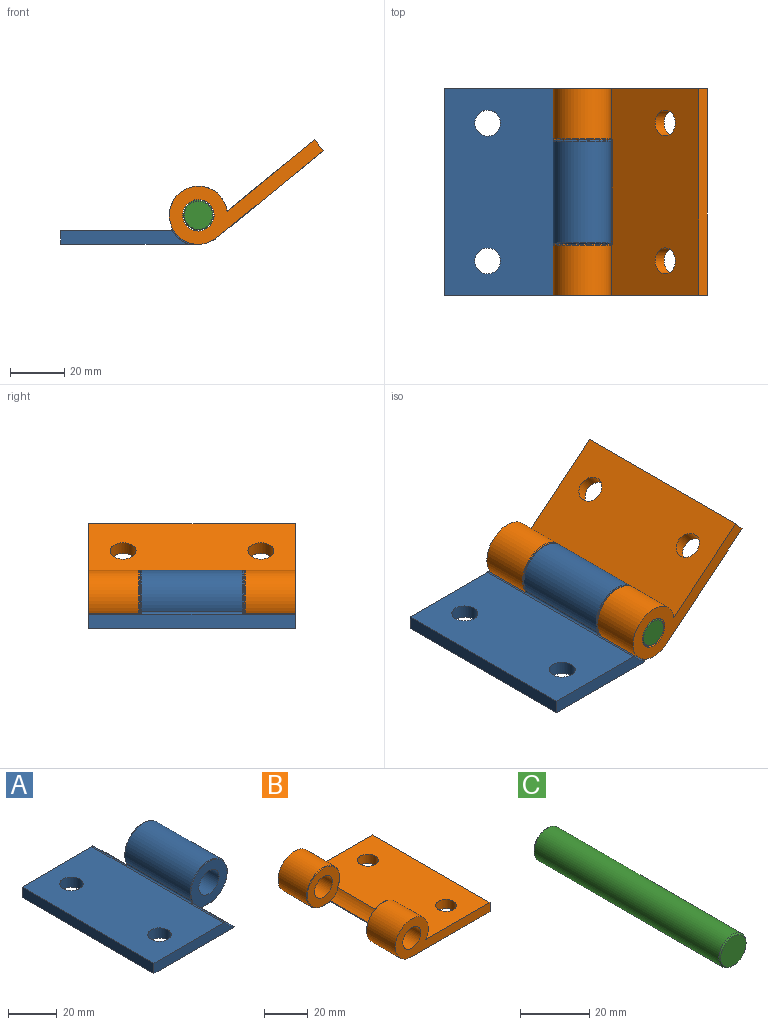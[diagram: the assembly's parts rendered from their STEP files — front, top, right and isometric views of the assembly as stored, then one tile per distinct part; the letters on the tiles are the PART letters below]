
ASSEMBLY  parts=3 mates=2
PART A: 23 faces, bbox 62.4x76.2x23.2 mm
  f0: cylinder r=1.59mm len=4.9mm, axis (-1,0,0), area 48.8mm2, adj f7,f8
  f1: cylinder r=4.76mm len=9.53mm, axis (0,0,1), area 154.3mm2, adj f10,f14
  f2: cylinder r=4.76mm len=9.53mm, axis (0,0,1), area 154.3mm2, adj f10,f14
  f3: torus R=10.45mm, axis (0,-1,0), area 21.8mm2, adj f4,f8,f16,f22
  f4: torus R=1.05mm, axis (0,-1,0), area 0.5mm2, adj f3,f11,f15,f16
  f5: torus R=10.45mm, axis (0,1,0), area 21.8mm2, adj f8,f18,f20,f21
  f6: cylinder r=0.25mm len=19.3mm, axis (0,-1,0), area 13.1mm2, adj f10,f12,f15,f16,f22
  f7: cylinder r=5.81mm len=38.1mm, axis (0,1,0), area 1382.9mm2, adj f0,f16,f18
  f8: cylinder r=10.71mm len=37.59mm, axis (0,1,0), area 2060.3mm2, adj f0,f3,f5,f10,f11
  f9: plane 46.2x5.37mm, normal (0,1,0), area 223.2mm2, adj f10,f11,f13,f14,f17,f19
  f10: plane 76.2x50.8mm, normal (0,0,-1), area 3541mm2, adj f1,f2,f6,f8,f9,f12,f13,f19
  f11: cylinder r=0.79mm len=76.2mm, axis (0,1,0), area 82.6mm2, adj f4,f8,f9,f12,f14,f15,f17,f21
  f12: plane 46.2x5.37mm, normal (0,-1,0), area 223.2mm2, adj f6,f10,f11,f13,f14,f15
  f13: plane 76.2x5.16mm, normal (-1,0,0), area 392.9mm2, adj f9,f10,f12,f14
  f14: plane 76.2x40.33mm, normal (0,0,1), area 2930.6mm2, adj f1,f2,f9,f11,f12,f13
  f15: cylinder r=11.27mm len=19.3mm, axis (0,-1,0), area 138mm2, adj f4,f6,f11,f12,f16
  f16: plane 20.9x20.9mm, normal (0,-1,0), area 244.4mm2, adj f3,f4,f6,f7,f15,f22
  f17: cylinder r=11.27mm len=19.3mm, axis (0,1,0), area 138mm2, adj f9,f11,f18,f19,f21
  f18: plane 20.9x20.9mm, normal (0,1,0), area 244.4mm2, adj f5,f7,f17,f19,f20,f21
  f19: cylinder r=0.25mm len=19.3mm, axis (0,1,0), area 13.1mm2, adj f9,f10,f17,f18,f20
  f20: cylinder r=0.25mm len=4.86mm, axis (1,0,0), area 1.9mm2, adj f5,f10,f18,f19
  f21: torus R=1.05mm, axis (0,1,0), area 0.5mm2, adj f5,f11,f17,f18
  f22: cylinder r=0.25mm len=4.86mm, axis (-1,0,0), area 1.9mm2, adj f3,f6,f10,f16
PART B: 19 faces, bbox 62.5x76.3x23.2 mm
  f0: cylinder r=4.76mm len=9.53mm, axis (0,0,1), area 154.3mm2, adj f10,f11
  f1: cylinder r=4.76mm len=9.53mm, axis (0,0,1), area 154.3mm2, adj f10,f11
  f2: torus R=10.45mm, axis (0,1,0), area 22.3mm2, adj f4,f11,f16,f18
  f3: cylinder r=5.81mm len=18.8mm, axis (0,1,0), area 686.2mm2, adj f16,f17
  f4: cylinder r=10.71mm len=21.41mm, axis (0,1,0), area 1043.7mm2, adj f2,f10,f11,f17
  f5: torus R=10.45mm, axis (0,-1,0), area 22.3mm2, adj f7,f8,f11,f15
  f6: cylinder r=5.81mm len=18.8mm, axis (0,-1,0), area 686.2mm2, adj f8,f12
  f7: cylinder r=10.71mm len=21.41mm, axis (0,-1,0), area 1043.7mm2, adj f5,f10,f11,f12
  f8: plane 20.9x20.9mm, normal (0,1,0), area 244.1mm2, adj f5,f6,f11,f13,f14,f15
  f9: plane 76.2x5.16mm, normal (1,0,0), area 392.9mm2, adj f10,f11,f12,f17
  f10: plane 76.2x50.8mm, normal (0,0,-1), area 3538.5mm2, adj f0,f1,f4,f7,f9,f12,f14,f15
  f11: plane 76.26x42.01mm, normal (0,0,1), area 3005.6mm2, adj f0,f1,f2,f4,f5,f7,f8,f9
  f12: plane 61.51x21.41mm, normal (0,-1,0), area 482.6mm2, adj f6,f7,f9,f10,f11
  f13: cylinder r=11.27mm len=38.61mm, axis (0,-1,0), area 270.2mm2, adj f8,f11,f14,f16
  f14: cylinder r=0.25mm len=39.12mm, axis (0,-1,0), area 26.6mm2, adj f8,f10,f13,f15,f16,f18
  f15: cylinder r=0.25mm len=4.86mm, axis (-1,0,0), area 1.9mm2, adj f5,f8,f10,f14
  f16: plane 20.9x20.9mm, normal (0,-1,0), area 244.1mm2, adj f2,f3,f11,f13,f14,f18
  f17: plane 61.51x21.41mm, normal (0,1,0), area 482.6mm2, adj f3,f4,f9,f10,f11
  f18: cylinder r=0.25mm len=4.86mm, axis (-1,0,0), area 1.9mm2, adj f2,f10,f14,f16
PART C: 5 faces, bbox 11.1x76.2x11.1 mm
  f0: cone r=5.56mm half-angle=45deg, axis (0,-1,0), area 18.2mm2, adj f2,f4
  f1: cone r=5.18mm half-angle=45deg, axis (0,1,0), area 18.2mm2, adj f2,f3
  f2: cylinder r=5.56mm len=75.44mm, axis (0,1,0), area 2633.6mm2, adj f0,f1
  f3: plane 10.35x10.35mm, normal (0,-1,0), area 84.1mm2, adj f1
  f4: plane 10.35x10.35mm, normal (0,1,0), area 84.1mm2, adj f0
PLACE A t=(-4.98,-5,7.28)mm fixed
PLACE B rot(axis=(0,-1,0),39.3deg) t=(-4.98,-5,7.28)mm
PLACE C rot(axis=(0,-1,0),11.3deg) t=(-4.98,-5,7.28)mm
MATE revolute C.f0 <-> A.f3  axis (0,1,0) through (-4.98,-5,7.28)mm
MATE revolute B.f2 <-> C.f0  axis (0,-1,0) through (-4.98,-43.1,7.28)mm
